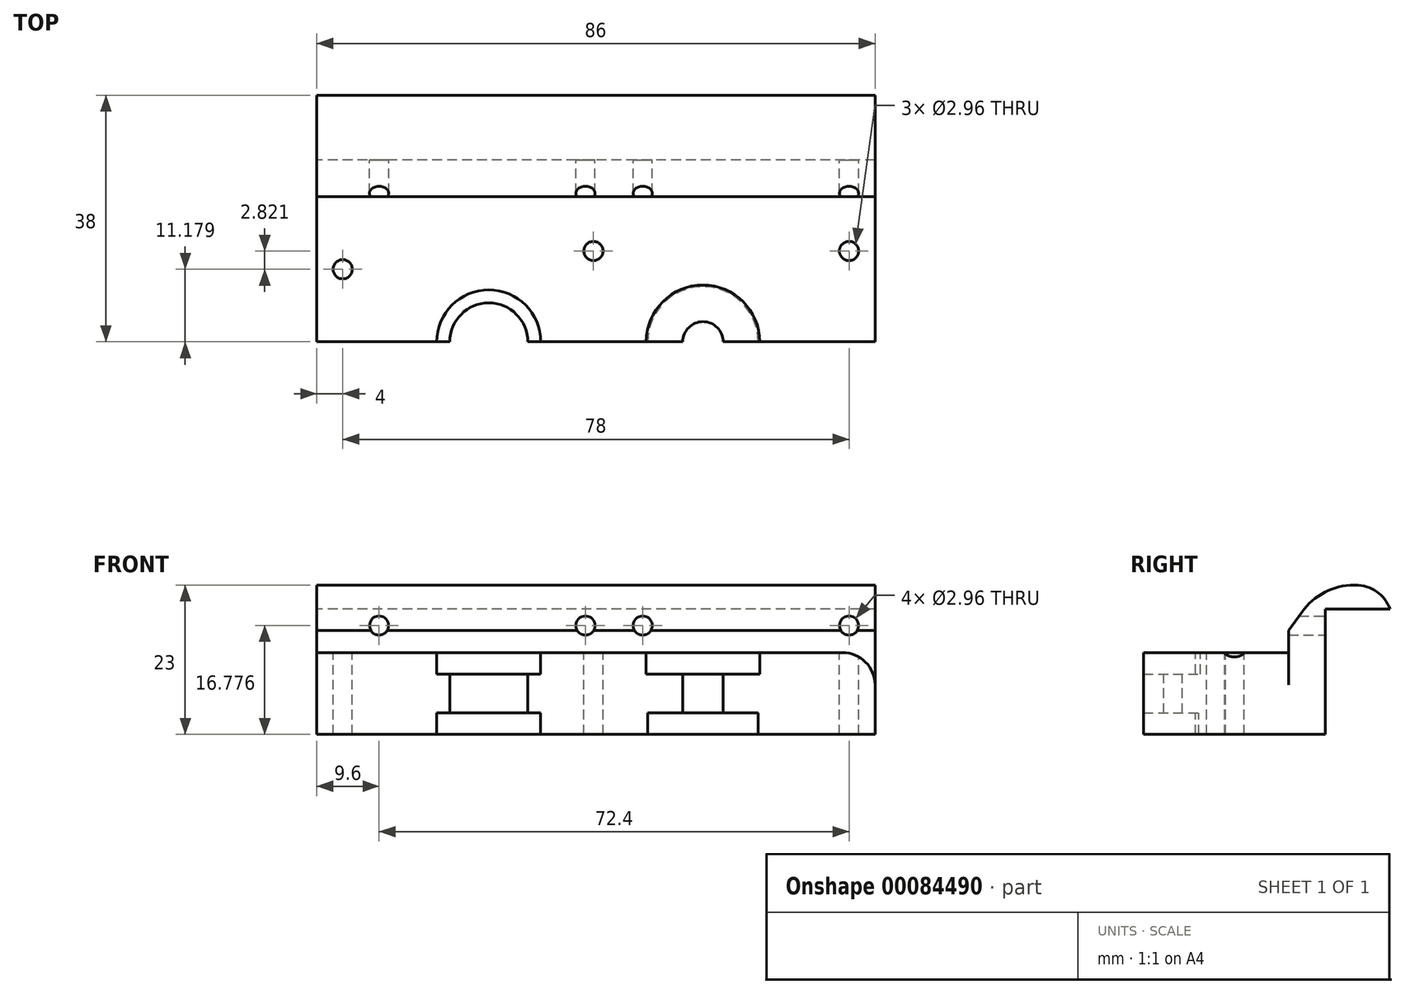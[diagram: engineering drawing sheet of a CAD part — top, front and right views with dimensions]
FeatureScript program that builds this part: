
annotation { "Feature Type Name" : "Feature", "Feature Type Description" : "" }
export const myFeature = defineFeature(function(context is Context, id is Id, definition is map)
    precondition{}
    {
        {
            var Q0;
            Q0=qCreatedBy(makeId("Top.planeOp"),FACE);
            var sketch = newSketch(context, id + "F0", { "sketchPlane" : qUnion([Q0])});
            skLineSegment(sketch, "E0.bottom", {"start": v(-34.44, 0) * mm, "end": v(51.56, 0) * mm});
            skLineSegment(sketch, "E0.top", {"start": v(-34.44, 40) * mm, "end": v(51.56, 40) * mm});
            skLineSegment(sketch, "E0.left", {"start": v(-34.44, 0) * mm, "end": v(-34.44, 40) * mm});
            skLineSegment(sketch, "E0.right", {"start": v(51.56, 0) * mm, "end": v(51.56, 40) * mm});
            skSolve(sketch);
        }
        {
            var Q0;
            Q0=makeQuery(id+"F0.imprint","IMPRINT",FACE,{"disambiguationData":[TD([[makeQuery(id+"F0.imprint","IMPRINT",EDGE,{"derivedFrom":sQuery(id+"F0.wireOp",EDGE,"E0.bottom")}),1.0]])]});
            extrude(context, id + "F1", {"entities" : qUnion([Q0]), "depth" : 19 * mm});
        }
        {
            var Q0;
            Q0=makeQuery(id+"F1.opExtrude","SWEPT_FACE",FACE,{"disambiguationData":[OSD([sQuery(id+"F0.wireOp",EDGE,"E0.left")])]});
            var sketch = newSketch(context, id + "F2", { "sketchPlane" : qUnion([Q0])});
            skLineSegment(sketch, "E1.bottom", {"start": v(-40, 0) * mm, "end": v(-28, 0) * mm});
            skLineSegment(sketch, "E1.top", {"start": v(-40, 16.78) * mm, "end": v(-28, 16.78) * mm});
            skLineSegment(sketch, "E1.left", {"start": v(-40, 0) * mm, "end": v(-40, 16.78) * mm});
            skLineSegment(sketch, "E1.right", {"start": v(-28, 0) * mm, "end": v(-28, 16.78) * mm});
            skLineSegment(sketch, "E2.bottom", {"start": v(-22.36, 19) * mm, "end": v(0, 19) * mm});
            skLineSegment(sketch, "E2.top", {"start": v(-22.36, 12.6) * mm, "end": v(0, 12.6) * mm});
            skLineSegment(sketch, "E2.left", {"start": v(-22.36, 19) * mm, "end": v(-22.36, 12.6) * mm});
            skLineSegment(sketch, "E2.right", {"start": v(0, 19) * mm, "end": v(0, 12.6) * mm});
            skSolve(sketch);
        }
        {
            var Q0;
            Q0 = qSketchRegion(id + "F2", true);
            extrude(context, id + "F3", {"entities" : qUnion([Q0]), "operationType" : NewBodyOperationType.REMOVE, "endBound" : BoundingType.THROUGH_ALL, "oppositeDirection" : true, "depth" : 25 * mm});
        }
        {
            var Q0;
            Q0=makeQuery(id+"F1.opExtrude","SWEPT_FACE",FACE,{"disambiguationData":[OSD([sQuery(id+"F0.wireOp",EDGE,"E0.bottom")])]});
            var sketch = newSketch(context, id + "F4", { "sketchPlane" : qUnion([Q0])});
            skLineSegment(sketch, "E3.bottom", {"start": v(25.06, 0) * mm, "end": v(-7.94, 0) * mm, "construction": true});
            skLineSegment(sketch, "E3.top", {"start": v(25.06, 25.2) * mm, "end": v(-7.94, 25.2) * mm, "construction": true});
            skLineSegment(sketch, "E3.left", {"start": v(25.06, 0) * mm, "end": v(25.06, 25.2) * mm, "construction": true});
            skLineSegment(sketch, "E3.right", {"start": v(-7.94, 0) * mm, "end": v(-7.94, 25.2) * mm, "construction": true});
            skPoint(sketch, "E3.middle", {"position": v(8.56, 12.6) * mm});
            skLineSegment(sketch, "E4.bottom", {"start": v(-7.94, 12.6) * mm, "end": v(0.06, 12.6) * mm});
            skLineSegment(sketch, "E4.top", {"start": v(-7.94, 0) * mm, "end": v(0.06, 0) * mm});
            skLineSegment(sketch, "E4.left", {"start": v(-7.94, 12.6) * mm, "end": v(-7.94, 0) * mm});
            skLineSegment(sketch, "E4.right", {"start": v(0.06, 12.6) * mm, "end": v(0.06, 0) * mm});
            skLineSegment(sketch, "E5.bottom", {"start": v(25.06, 12.6) * mm, "end": v(33.56, 12.6) * mm});
            skLineSegment(sketch, "E5.top", {"start": v(25.06, 0) * mm, "end": v(33.56, 0) * mm});
            skLineSegment(sketch, "E5.left", {"start": v(25.06, 12.6) * mm, "end": v(25.06, 0) * mm});
            skLineSegment(sketch, "E5.right", {"start": v(33.56, 12.6) * mm, "end": v(33.56, 0) * mm});
            skLineSegment(sketch, "E6", {"start": v(-34.44, 6.3) * mm, "end": v(61.77, 6.3) * mm, "construction": true});
            skPoint(sketch, "E6.endSnap0", {"position": v(51.56, 6.3) * mm});
            skLineSegment(sketch, "E7.bottom", {"start": v(-1.94, 9.3) * mm, "end": v(-13.94, 9.3) * mm});
            skLineSegment(sketch, "E7.top", {"start": v(-1.94, 3.3) * mm, "end": v(-13.94, 3.3) * mm});
            skLineSegment(sketch, "E7.left", {"start": v(-1.94, 9.3) * mm, "end": v(-1.94, 3.3) * mm});
            skLineSegment(sketch, "E7.right", {"start": v(-13.94, 9.3) * mm, "end": v(-13.94, 3.3) * mm});
            skPoint(sketch, "E7.middle", {"position": v(-7.94, 6.3) * mm});
            skLineSegment(sketch, "E8.bottom", {"start": v(28.17, 9.3) * mm, "end": v(38.95, 9.3) * mm});
            skLineSegment(sketch, "E8.top", {"start": v(28.17, 3.3) * mm, "end": v(38.95, 3.3) * mm});
            skLineSegment(sketch, "E8.left", {"start": v(28.17, 9.3) * mm, "end": v(28.17, 3.3) * mm});
            skLineSegment(sketch, "E8.right", {"start": v(38.95, 9.3) * mm, "end": v(38.95, 3.3) * mm});
            skPoint(sketch, "E8.middle", {"position": v(33.56, 6.3) * mm});
            skLineSegment(sketch, "E9", {"start": v(-1.94, 9.3) * mm, "end": v(0.06, 9.3) * mm});
            skLineSegment(sketch, "E10", {"start": v(0.06, 9.3) * mm, "end": v(0.06, 3.3) * mm});
            skLineSegment(sketch, "E11", {"start": v(0.06, 3.3) * mm, "end": v(-1.94, 3.3) * mm});
            skLineSegment(sketch, "E12", {"start": v(28.17, 9.3) * mm, "end": v(25.06, 9.3) * mm});
            skLineSegment(sketch, "E13", {"start": v(25.06, 9.3) * mm, "end": v(25.06, 3.3) * mm});
            skLineSegment(sketch, "E14", {"start": v(25.06, 3.3) * mm, "end": v(28.17, 3.3) * mm});
            skSolve(sketch);
        }
        {
            var Q0;
            {var subQ5=sQuery(id+"F4.wireOp",EDGE,"E4.bottom");Q0=makeQuery(id+"F4.imprint","IMPRINT",FACE,{"disambiguationData":[TD([[makeQuery(id+"F4.imprint","IMPRINT",EDGE,{"derivedFrom":subQ5}),1.0]])]});}
            var Q1;
            {var subQ5=sQuery(id+"F4.wireOp",EDGE,"E4.top");Q1=makeQuery(id+"F4.imprint","IMPRINT",FACE,{"disambiguationData":[TD([[makeQuery(id+"F4.imprint","IMPRINT",EDGE,{"derivedFrom":subQ5}),1.0]])]});}
            var Q2;
            {var subQ5=sQuery(id+"F4.wireOp",EDGE,"E7.left");Q2=makeQuery(id+"F4.imprint","IMPRINT",FACE,{"disambiguationData":[TD([[makeQuery(id+"F4.imprint","IMPRINT",EDGE,{"derivedFrom":subQ5}),-1.0]])]});}
            var Q3;
            Q3=sQuery(id+"F4.wireOp",EDGE,"E3.right");
            revolve(context, id + "F5", {"operationType" : NewBodyOperationType.REMOVE, "entities" : qUnion([Q0, Q1, Q2]), "axis" : qUnion([Q3]), "revolveType" : RevolveType.FULL, "oppositeDirection" : true});
        }
        {
            var Q0;
            {var subQ3=sQuery(id+"F0.wireOp",EDGE,"E0.bottom");var subQ6=sQuery(id+"F0.wireOp",EDGE,"E0.right");Q0=makeQuery(id+"F5.boolean.opBoolean","SPLIT",FACE,{"disambiguationData":[TD([makeQuery(id+"F1.opExtrude","SWEPT_FACE",FACE,{"disambiguationData":[OSD([subQ6])]})])],"derivedFrom":makeQuery(id+"F1.opExtrude","SWEPT_FACE",FACE,{"disambiguationData":[OSD([subQ3])]})});}
            var sketch = newSketch(context, id + "F6", { "sketchPlane" : qUnion([Q0])});
            skLineSegment(sketch, "E15.bottom", {"start": v(33.8, 12.6) * mm, "end": v(25.8, 12.6) * mm});
            skLineSegment(sketch, "E15.top", {"start": v(33.8, 0) * mm, "end": v(25.8, 0) * mm});
            skLineSegment(sketch, "E15.left", {"start": v(33.8, 12.6) * mm, "end": v(33.8, 9.3) * mm});
            skLineSegment(sketch, "E15.right", {"start": v(25.8, 12.6) * mm, "end": v(25.8, 0) * mm});
            skLineSegment(sketch, "E16.top", {"start": v(33.8, 3.3) * mm, "end": v(25.8, 3.3) * mm});
            skLineSegment(sketch, "E16.right", {"start": v(25.8, 6.3) * mm, "end": v(25.8, 3.3) * mm});
            skLineSegment(sketch, "E17.top", {"start": v(25.8, 9.3) * mm, "end": v(33.8, 9.3) * mm});
            skLineSegment(sketch, "E17.left", {"start": v(25.8, 6.3) * mm, "end": v(25.8, 9.3) * mm});
            skLineSegment(sketch, "E18.bottom", {"start": v(26.03, 9.3) * mm, "end": v(33.8, 9.3) * mm});
            skLineSegment(sketch, "E18.top", {"start": v(26.03, 3.3) * mm, "end": v(33.8, 3.3) * mm});
            skLineSegment(sketch, "E19.bottom", {"start": v(25.8, 9.3) * mm, "end": v(31.8, 9.3) * mm});
            skLineSegment(sketch, "E19.top", {"start": v(25.8, 3.3) * mm, "end": v(31.8, 3.3) * mm});
            skLineSegment(sketch, "E19.left", {"start": v(25.8, 9.3) * mm, "end": v(25.8, 3.3) * mm});
            skLineSegment(sketch, "E19.right", {"start": v(31.8, 9.3) * mm, "end": v(31.8, 3.3) * mm});
            skLineSegment(sketch, "E20.trimOffspring", {"start": v(33.8, 3.3) * mm, "end": v(33.8, 0) * mm});
            skPoint(sketch, "E16.left.start.orphan", {"position": v(33.8, 6.3) * mm});
            skLineSegment(sketch, "E21", {"start": v(25.8, 0) * mm, "end": v(33.8, 0) * mm});
            skSolve(sketch);
        }
        {
            var Q0;
            Q0=makeQuery(id+"F4.imprint","IMPRINT",FACE,{"disambiguationData":[TD([[makeQuery(id+"F4.imprint","IMPRINT",EDGE,{"derivedFrom":sQuery(id+"F4.wireOp",EDGE,"E8.left")}),-1.0]])]});
            var Q1;
            {var subQ1=sQuery(id+"F4.wireOp",EDGE,"E5.bottom");Q1=makeQuery(id+"F4.imprint","IMPRINT",FACE,{"disambiguationData":[TD([[makeQuery(id+"F4.imprint","IMPRINT",EDGE,{"derivedFrom":subQ1}),1.0]])]});}
            var Q2;
            {var subQ4=sQuery(id+"F4.wireOp",EDGE,"E5.top");Q2=makeQuery(id+"F4.imprint","IMPRINT",FACE,{"disambiguationData":[TD([[makeQuery(id+"F4.imprint","IMPRINT",EDGE,{"derivedFrom":subQ4}),1.0]])]});}
            var Q3;
            {var subQ1=sQuery(id+"F6.wireOp",EDGE,"E15.bottom");Q3=makeQuery(id+"F6.imprint","IMPRINT",FACE,{"disambiguationData":[TD([[makeQuery(id+"F6.imprint","IMPRINT",EDGE,{"derivedFrom":subQ1}),1.0]])]});}
            var Q4;
            {var subQ3=sQuery(id+"F6.wireOp",EDGE,"E19.top");Q4=makeQuery(id+"F6.imprint","IMPRINT",FACE,{"disambiguationData":[TD([[makeQuery(id+"F6.imprint","IMPRINT",EDGE,{"derivedFrom":subQ3}),-1.0]])]});}
            var Q5;
            {var subQ1=sQuery(id+"F6.wireOp",EDGE,"E19.bottom");Q5=makeQuery(id+"F6.imprint","IMPRINT",FACE,{"disambiguationData":[TD([[makeQuery(id+"F6.imprint","IMPRINT",EDGE,{"derivedFrom":subQ1}),-1.0]])]});}
            var Q6;
            Q6=sQuery(id+"F4.wireOp",EDGE,"E3.left");
            revolve(context, id + "F7", {"operationType" : NewBodyOperationType.REMOVE, "entities" : qUnion([Q0, Q1, Q2, Q3, Q4, Q5]), "axis" : qUnion([Q6]), "revolveType" : RevolveType.FULL, "oppositeDirection" : true});
        }
        {
            var Q0;
            Q0=makeQuery(id+"F1.opExtrude","CAP_EDGE",EDGE,{"disambiguationData":[OSD([sQuery(id+"F0.wireOp",EDGE,"E0.top")])],"isStart":false});
            fillet(context, id + "F8", {"entities" : qUnion([Q0]), "radius" : 18.28 * mm, "tangentPropagation" : true, "allowEdgeOverflow" : false});
        }
        {
            var Q0;
            Q0=makeQuery(id+"F3.boolean.opBoolean","COPY",FACE,{"derivedFrom":makeQuery(id+"F3.opExtrude","SWEPT_FACE",FACE,{"disambiguationData":[OSD([sQuery(id+"F2.wireOp",EDGE,"E1.right")])]})});
            var sketch = newSketch(context, id + "F9", { "sketchPlane" : qUnion([Q0])});
            skLineSegment(sketch, "E22.bottom", {"start": v(-51.56, 16.78) * mm, "end": v(34.44, 16.78) * mm, "construction": true});
            skLineSegment(sketch, "E22.top", {"start": v(-51.56, 16.78) * mm, "end": v(34.44, 16.78) * mm, "construction": true});
            skLineSegment(sketch, "E22.left", {"start": v(-51.56, 16.78) * mm, "end": v(-51.56, 16.78) * mm});
            skLineSegment(sketch, "E22.right", {"start": v(34.44, 16.78) * mm, "end": v(34.44, 16.78) * mm});
            skCircle(sketch, "E23", {"center": v(-47.56, 16.78) * mm, "radius": 1.48 * mm});
            skCircle(sketch, "E24", {"center": v(-15.77, 16.78) * mm, "radius": 1.48 * mm});
            skCircle(sketch, "E25", {"center": v(-6.95, 16.78) * mm, "radius": 1.48 * mm});
            skCircle(sketch, "E26", {"center": v(24.84, 16.78) * mm, "radius": 1.48 * mm});
            skSolve(sketch);
        }
        {
            var Q0;
            Q0 = qSketchRegion(id + "F9", true);
            extrude(context, id + "F10", {"entities" : qUnion([Q0]), "operationType" : NewBodyOperationType.REMOVE, "endBound" : BoundingType.SYMMETRIC, "oppositeDirection" : true, "depth" : 27.23 * mm});
        }
        {
            var Q0;
            Q0=makeQuery(id+"F3.boolean.opBoolean","COPY",FACE,{"derivedFrom":makeQuery(id+"F3.opExtrude","SWEPT_FACE",FACE,{"disambiguationData":[OSD([sQuery(id+"F2.wireOp",EDGE,"E2.top")])]})});
            var sketch = newSketch(context, id + "F11", { "sketchPlane" : qUnion([Q0])});
            skLineSegment(sketch, "E27.bottom", {"start": v(-34.44, 22.36) * mm, "end": v(-30.44, 22.36) * mm, "construction": true});
            skLineSegment(sketch, "E27.top", {"start": v(-34.44, 0) * mm, "end": v(-30.44, 0) * mm, "construction": true});
            skLineSegment(sketch, "E27.left", {"start": v(-34.44, 22.36) * mm, "end": v(-34.44, 0) * mm, "construction": true});
            skLineSegment(sketch, "E27.right", {"start": v(-30.44, 22.36) * mm, "end": v(-30.44, 0) * mm, "construction": true});
            skLineSegment(sketch, "E28.bottom", {"start": v(51.56, 0) * mm, "end": v(47.56, 0) * mm, "construction": true});
            skLineSegment(sketch, "E28.top", {"start": v(51.56, 28) * mm, "end": v(47.56, 28) * mm, "construction": true});
            skLineSegment(sketch, "E28.left", {"start": v(51.56, 0) * mm, "end": v(51.56, 28) * mm, "construction": true});
            skLineSegment(sketch, "E28.right", {"start": v(47.56, 0) * mm, "end": v(47.56, 28) * mm, "construction": true});
            skCircle(sketch, "E29", {"center": v(-30.44, 11.18) * mm, "radius": 1.48 * mm});
            skCircle(sketch, "E30", {"center": v(47.56, 14) * mm, "radius": 1.48 * mm});
            skCircle(sketch, "E31", {"center": v(8.18, 14) * mm, "radius": 1.48 * mm});
            skPoint(sketch, "E31.centerSnap0", {"position": v(8.18, 0) * mm});
            skSolve(sketch);
        }
        {
            var Q0;
            Q0 = qSketchRegion(id + "F11", true);
            extrude(context, id + "F12", {"entities" : qUnion([Q0]), "operationType" : NewBodyOperationType.REMOVE, "endBound" : BoundingType.THROUGH_ALL, "oppositeDirection" : true, "depth" : 25 * mm});
        }
        {
            var Q0;
            Q0=makeQuery(id+"F3.boolean.opBoolean","COPY",EDGE,{"derivedFrom":makeQuery(id+"F3.opExtrude","CAP_EDGE",EDGE,{"disambiguationData":[OSD([sQuery(id+"F2.wireOp",EDGE,"E2.top")])],"isStart":true})});
            var Q1;
            Q1=makeQuery(id+"F3.boolean.opBoolean","INTERSECT",EDGE,{"derivedFrom":[makeQuery(id+"F1.opExtrude","SWEPT_FACE",FACE,{"disambiguationData":[OSD([sQuery(id+"F0.wireOp",EDGE,"E0.right")])]}),makeQuery(id+"F3.opExtrude","SWEPT_FACE",FACE,{"disambiguationData":[OSD([sQuery(id+"F2.wireOp",EDGE,"E2.top")])]})]});
            fillet(context, id + "F13", {"entities" : qUnion([Q0, Q1]), "radius" : 5 * mm, "tangentPropagation" : true, "allowEdgeOverflow" : false});
        }
        {
            var Q0;
            Q0=makeQuery(id+"F1.opExtrude","SWEPT_FACE",FACE,{"disambiguationData":[OSD([sQuery(id+"F0.wireOp",EDGE,"E0.right")])]});
            var sketch = newSketch(context, id + "F14", { "sketchPlane" : qUnion([Q0])});
            skLineSegment(sketch, "E32.bottom", {"start": v(28, 16.78) * mm, "end": v(40.27, 16.78) * mm});
            skLineSegment(sketch, "E32.top", {"start": v(28, 19.78) * mm, "end": v(40.27, 19.78) * mm});
            skLineSegment(sketch, "E32.left", {"start": v(28, 16.78) * mm, "end": v(28, 19.78) * mm});
            skLineSegment(sketch, "E32.right", {"start": v(40.27, 16.78) * mm, "end": v(40.27, 19.78) * mm});
            skSolve(sketch);
        }
        {
            var Q0;
            Q0 = qSketchRegion(id + "F14", true);
            extrude(context, id + "F15", {"entities" : qUnion([Q0]), "operationType" : NewBodyOperationType.REMOVE, "endBound" : BoundingType.THROUGH_ALL, "oppositeDirection" : true, "depth" : 25 * mm});
        }
        {
            var Q0;
            Q0=makeQuery(id+"F1.opExtrude","CAP_FACE",FACE,{"disambiguationData":[OSD([sQuery(id+"F0.wireOp",EDGE,"E0.bottom"),sQuery(id+"F0.wireOp",EDGE,"E0.top"),sQuery(id+"F0.wireOp",EDGE,"E0.left"),sQuery(id+"F0.wireOp",EDGE,"E0.right")])],"isStart":false});
            var sketch = newSketch(context, id + "F16", { "sketchPlane" : qUnion([Q0])});
            skLineSegment(sketch, "E33.bottom", {"start": v(-34.44, 28) * mm, "end": v(51.56, 28) * mm});
            skLineSegment(sketch, "E33.top", {"start": v(-34.44, 22.36) * mm, "end": v(51.56, 22.36) * mm});
            skLineSegment(sketch, "E33.left", {"start": v(-34.44, 28) * mm, "end": v(-34.44, 22.36) * mm});
            skLineSegment(sketch, "E33.right", {"start": v(51.56, 28) * mm, "end": v(51.56, 22.36) * mm});
            skSolve(sketch);
        }
        {
            var Q0;
            Q0 = qSketchRegion(id + "F16", true);
            extrude(context, id + "F17", {"entities" : qUnion([Q0]), "operationType" : NewBodyOperationType.ADD, "depth" : 4 * mm});
        }
        {
            var Q0;
            Q0=makeQuery(id+"F17.boolean.opBoolean","MERGE",FACE,{"derivedFrom":[makeQuery(id+"F15.boolean.opBoolean","MERGE",FACE,{"derivedFrom":[makeQuery(id+"F3.boolean.opBoolean","COPY",FACE,{"derivedFrom":makeQuery(id+"F3.opExtrude","SWEPT_FACE",FACE,{"disambiguationData":[OSD([sQuery(id+"F2.wireOp",EDGE,"E1.right")])]})}),makeQuery(id+"F15.opExtrude","SWEPT_FACE",FACE,{"disambiguationData":[OSD([sQuery(id+"F14.wireOp",EDGE,"E32.left")])]})]}),makeQuery(id+"F17.opExtrude","SWEPT_FACE",FACE,{"disambiguationData":[OSD([sQuery(id+"F16.wireOp",EDGE,"E33.bottom")])]})]});
            var sketch = newSketch(context, id + "F18", { "sketchPlane" : qUnion([Q0])});
            skLineSegment(sketch, "E34.bottom", {"start": v(-51.56, 23) * mm, "end": v(34.44, 23) * mm});
            skLineSegment(sketch, "E34.top", {"start": v(-51.56, 19.3) * mm, "end": v(34.44, 19.3) * mm});
            skLineSegment(sketch, "E34.left", {"start": v(-51.56, 23) * mm, "end": v(-51.56, 19.3) * mm});
            skLineSegment(sketch, "E34.right", {"start": v(34.44, 23) * mm, "end": v(34.44, 19.3) * mm});
            skSolve(sketch);
        }
        {
            var Q0;
            Q0 = qSketchRegion(id + "F18", true);
            extrude(context, id + "F19", {"entities" : qUnion([Q0]), "operationType" : NewBodyOperationType.ADD, "depth" : 10 * mm});
        }
        {
            var Q0;
            Q0=makeQuery(id+"F17.opExtrude","CAP_EDGE",EDGE,{"disambiguationData":[OSD([sQuery(id+"F16.wireOp",EDGE,"E33.top")])],"isStart":false});
            chamfer(context, id + "F20", {"entities" : qUnion([Q0]), "chamferType" : ChamferType.TWO_OFFSETS, "width1" : 7 * mm, "oppositeDirection" : false, "width2" : 5 * mm, "tangentPropagation" : true});
        }
        {
            var Q0;
            {var subQ0=sQuery(id+"F16.wireOp",EDGE,"E33.top");Q0=makeQuery(id+"F20.opChamfer","BLEND_EDGE",EDGE,{"blendedFrom":[makeQuery(id+"F17.opExtrude","CAP_EDGE",EDGE,{"disambiguationData":[OSD([subQ0])],"isStart":false}),makeQuery(id+"F19.boolean.opBoolean","MERGE",FACE,{"derivedFrom":[makeQuery(id+"F17.opExtrude","CAP_FACE",FACE,{"disambiguationData":[OSD([sQuery(id+"F16.wireOp",EDGE,"E33.bottom"),subQ0,sQuery(id+"F16.wireOp",EDGE,"E33.left"),sQuery(id+"F16.wireOp",EDGE,"E33.right")])],"isStart":false}),makeQuery(id+"F19.opExtrude","SWEPT_FACE",FACE,{"disambiguationData":[OSD([sQuery(id+"F18.wireOp",EDGE,"E34.bottom")])]})]})],"blendedInto":[makeQuery(id+"F19.boolean.opBoolean","MERGE",FACE,{"derivedFrom":[makeQuery(id+"F17.opExtrude","CAP_FACE",FACE,{"disambiguationData":[OSD([sQuery(id+"F16.wireOp",EDGE,"E33.bottom"),subQ0,sQuery(id+"F16.wireOp",EDGE,"E33.left"),sQuery(id+"F16.wireOp",EDGE,"E33.right")])],"isStart":false}),makeQuery(id+"F19.opExtrude","SWEPT_FACE",FACE,{"disambiguationData":[OSD([sQuery(id+"F18.wireOp",EDGE,"E34.bottom")])]})]})]});}
            fillet(context, id + "F21", {"entities" : qUnion([Q0]), "radius" : 9.95 * mm, "tangentPropagation" : true, "allowEdgeOverflow" : false});
        }
        {
            var Q0;
            Q0=makeQuery(id+"F19.opExtrude","CAP_EDGE",EDGE,{"disambiguationData":[OSD([sQuery(id+"F18.wireOp",EDGE,"E34.bottom")])],"isStart":false});
            fillet(context, id + "F22", {"entities" : qUnion([Q0]), "radius" : 5.68 * mm, "tangentPropagation" : true, "allowEdgeOverflow" : false});
        }
    });
